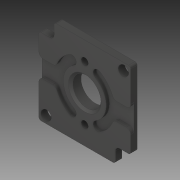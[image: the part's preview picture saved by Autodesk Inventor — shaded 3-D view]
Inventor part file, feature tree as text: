
AUTODESK INVENTOR PART (.ipt)
format: ipt  version: 2019 (Build 230136000, 136)  size: 252,416 bytes
history: native  units: in
note: dims shown in document units (in); Inventor stores cm internally (conversion verified against a paired STEP export)
features: fillet x1
ambient origin geometry x8: Origin, YZ Plane, XZ Plane, XY Plane, X Axis, Y Axis, Z Axis, Center Point
bodies: Solid1 (feature_tree)
feature tree (1):
  fillet  "Fillet4"  [1 undecoded]
note: 1 required parameter value undecoded (feature->parameter linkage not recoverable at this tier; creation-order binding heuristic only, values carry confidence <= 0.55)
